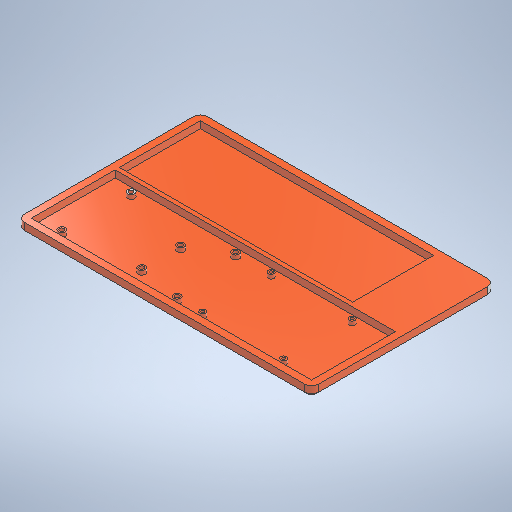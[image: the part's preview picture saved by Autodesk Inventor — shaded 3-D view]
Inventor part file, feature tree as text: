
AUTODESK INVENTOR PART (.ipt)
format: ipt  version: 2025.2 (Build 292293000, 293)  size: 346,624 bytes
history: native  units: mm
features: extrude x3, sketch x1, fillet x1, chamfer x1
ambient origin geometry x8: Origin, YZ Plane, XZ Plane, XY Plane, X Axis, Y Axis, Z Axis, Center Point
bodies: Solid1 (feature_tree)
feature tree (6):
  sketch  "Sketch1"  dims[d8=85.0mm d9=56.0mm d10=2.2mm d11=3.5mm d12=3.5mm d13=3.5mm d19=2.0mm d20=0.0mm d21=5.0mm d22=0.0mm d29=1.0mm d33=1.0mm d34=1.0mm d35=1.0mm d36=1.0mm d37=3.0mm d38=0.0mm d39=5.0mm d44=58.0mm d45=2.0mm d46=2.0mm d47=45.0deg d48=53.34mm d49=101.6mm d50=167.0mm d51=58.0mm d52=5.0mm d55=2.0mm d56=2.0mm d57=2.0mm d58=10.0mm d59=5.0mm d60=15.24mm d61=2.54mm d62=3.1mm d63=1.0mm d64=90.17mm d65=13.97mm d66=96.52mm d68=66.04mm d70=45.72mm d71=17.78mm d73=5.0mm d74=50.8mm d76=3.0mm d77=2.0mm d78=5.0mm d75=0.872665mm]
  extrude  "Extrusion1"  Depth=5.0mm
  extrude  "Extrusion2"  Depth=5.0mm
  extrude  "Extrusion3"  Depth=5.0mm
  fillet  "Fillet1"  Radius=3.5mm
  chamfer  "Chamfer1"  Distance=3.5mm
